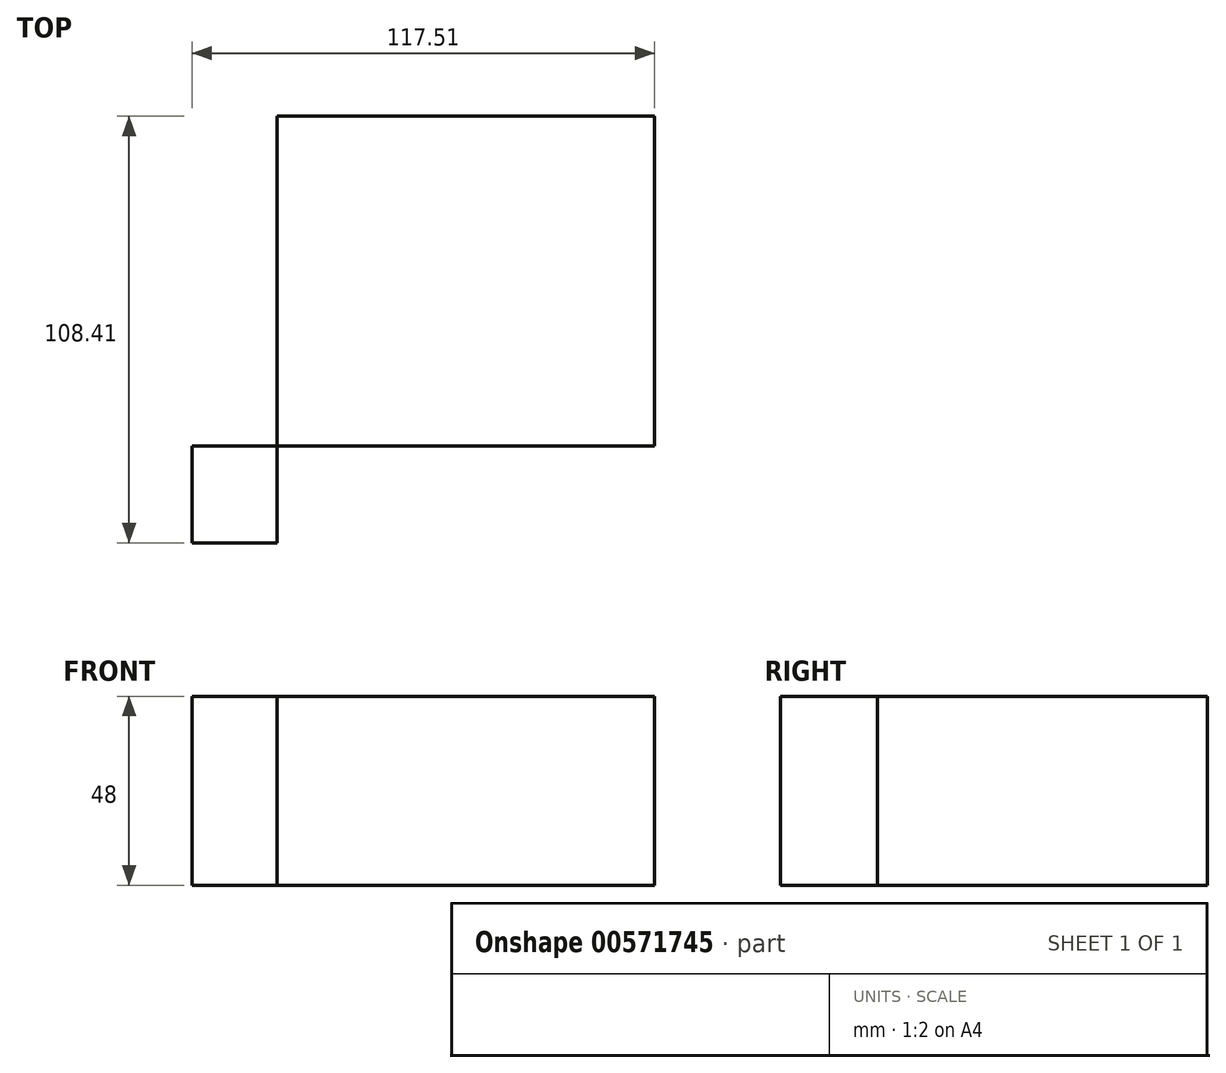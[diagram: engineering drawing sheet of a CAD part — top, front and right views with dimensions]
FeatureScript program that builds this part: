
annotation { "Feature Type Name" : "Feature", "Feature Type Description" : "" }
export const myFeature = defineFeature(function(context is Context, id is Id, definition is map)
    precondition{}
    {
        {
            var Q0;
            Q0=qCreatedBy(makeId("Top.planeOp"),FACE);
            var sketch = newSketch(context, id + "F0", { "sketchPlane" : qUnion([Q0])});
            skLineSegment(sketch, "E0.bottom", {"start": v(-33.73, 36.02) * mm, "end": v(62.18, 36.02) * mm});
            skLineSegment(sketch, "E0.top", {"start": v(-33.73, -47.82) * mm, "end": v(62.18, -47.82) * mm});
            skLineSegment(sketch, "E0.left", {"start": v(-33.73, 36.02) * mm, "end": v(-33.73, -47.82) * mm});
            skLineSegment(sketch, "E0.right", {"start": v(62.18, 36.02) * mm, "end": v(62.18, -47.82) * mm});
            skLineSegment(sketch, "E1.bottom", {"start": v(-33.73, -47.82) * mm, "end": v(-55.33, -47.82) * mm});
            skLineSegment(sketch, "E1.top", {"start": v(-33.73, -72.39) * mm, "end": v(-55.33, -72.39) * mm});
            skLineSegment(sketch, "E1.left", {"start": v(-33.73, -47.82) * mm, "end": v(-33.73, -72.39) * mm});
            skLineSegment(sketch, "E1.right", {"start": v(-55.33, -47.82) * mm, "end": v(-55.33, -72.39) * mm});
            skSolve(sketch);
        }
        {
            var Q0;
            Q0 = qSketchRegion(id + "F0", true);
            extrude(context, id + "F1", {"entities" : qUnion([Q0]), "depth" : 48 * mm, "offsetDistance" : 25 * mm});
        }
    });
